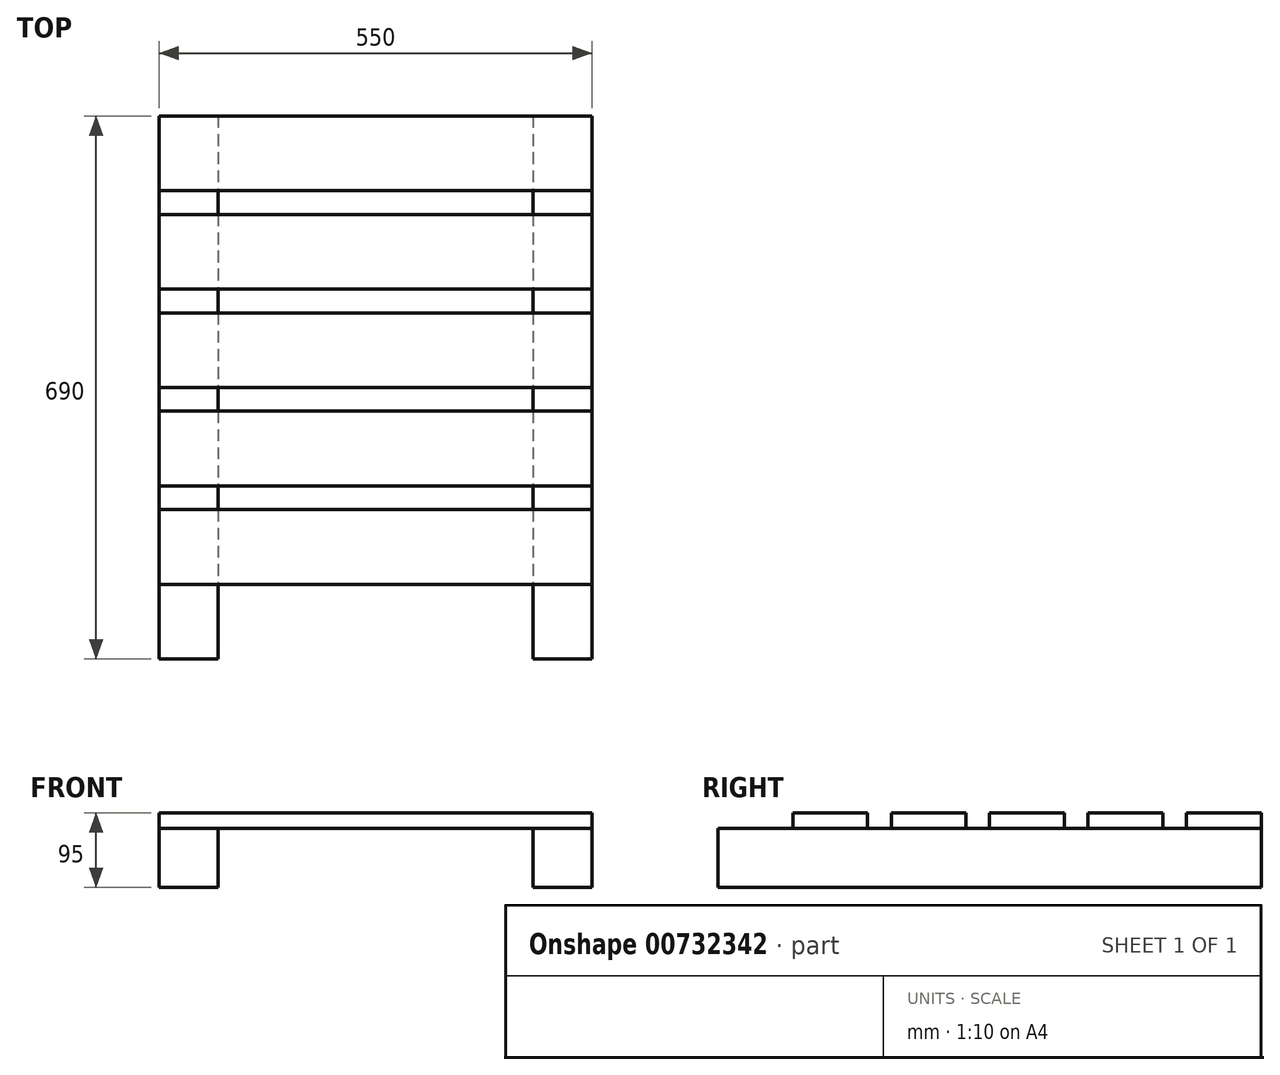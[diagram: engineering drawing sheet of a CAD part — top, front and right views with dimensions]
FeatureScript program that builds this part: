
annotation { "Feature Type Name" : "Feature", "Feature Type Description" : "" }
export const myFeature = defineFeature(function(context is Context, id is Id, definition is map)
    precondition{}
    {
        {
            var Q0;
            Q0=qCreatedBy(makeId("Top.planeOp"),FACE);
            var sketch = newSketch(context, id + "F0", { "sketchPlane" : qUnion([Q0])});
            skLineSegment(sketch, "E0.bottom", {"start": v(-275, -300) * mm, "end": v(275, -300) * mm, "construction": true});
            skLineSegment(sketch, "E0.top", {"start": v(-275, 300) * mm, "end": v(275, 300) * mm, "construction": true});
            skLineSegment(sketch, "E0.left", {"start": v(-275, -300) * mm, "end": v(-275, 300) * mm, "construction": true});
            skLineSegment(sketch, "E0.right", {"start": v(275, -300) * mm, "end": v(275, 300) * mm, "construction": true});
            skPoint(sketch, "E0.middle", {"position": v(0, 0) * mm});
            skLineSegment(sketch, "E1.bottom", {"start": v(-275, 300) * mm, "end": v(275, 300) * mm});
            skLineSegment(sketch, "E1.top", {"start": v(-275, 205) * mm, "end": v(275, 205) * mm});
            skLineSegment(sketch, "E1.left", {"start": v(-275, 300) * mm, "end": v(-275, 205) * mm});
            skLineSegment(sketch, "E1.right", {"start": v(275, 300) * mm, "end": v(275, 205) * mm});
            skLineSegment(sketch, "E2", {"start": v(-275, 205) * mm, "end": v(-275, 175) * mm, "construction": true});
            skLineSegment(sketch, "E3", {"start": v(-275, 175) * mm, "end": v(-275, 80) * mm, "construction": true});
            skLineSegment(sketch, "E4", {"start": v(-275, 80) * mm, "end": v(-275, 50) * mm, "construction": true});
            skLineSegment(sketch, "E5", {"start": v(-275, 50) * mm, "end": v(-275, -45) * mm, "construction": true});
            skLineSegment(sketch, "E6", {"start": v(-275, -45) * mm, "end": v(-275, -75) * mm, "construction": true});
            skLineSegment(sketch, "E7", {"start": v(-275, -75) * mm, "end": v(-275, -170) * mm, "construction": true});
            skLineSegment(sketch, "E8", {"start": v(-275, -170) * mm, "end": v(-275, -200) * mm, "construction": true});
            skLineSegment(sketch, "E9", {"start": v(-275, -200) * mm, "end": v(-275, -295) * mm, "construction": true});
            skLineSegment(sketch, "E10.bottom", {"start": v(-275, 175) * mm, "end": v(275, 175) * mm});
            skLineSegment(sketch, "E10.top", {"start": v(-275, 80) * mm, "end": v(275, 80) * mm});
            skLineSegment(sketch, "E10.left", {"start": v(-275, 175) * mm, "end": v(-275, 80) * mm});
            skLineSegment(sketch, "E10.right", {"start": v(275, 175) * mm, "end": v(275, 80) * mm});
            skLineSegment(sketch, "E11.bottom", {"start": v(-275, 50) * mm, "end": v(275, 50) * mm});
            skLineSegment(sketch, "E11.top", {"start": v(-275, -45) * mm, "end": v(275, -45) * mm});
            skLineSegment(sketch, "E11.left", {"start": v(-275, 50) * mm, "end": v(-275, -45) * mm});
            skLineSegment(sketch, "E11.right", {"start": v(275, 50) * mm, "end": v(275, -45) * mm});
            skLineSegment(sketch, "E12.bottom", {"start": v(-275, -75) * mm, "end": v(275, -75) * mm});
            skLineSegment(sketch, "E12.top", {"start": v(-275, -170) * mm, "end": v(275, -170) * mm});
            skLineSegment(sketch, "E12.left", {"start": v(-275, -75) * mm, "end": v(-275, -170) * mm});
            skLineSegment(sketch, "E12.right", {"start": v(275, -75) * mm, "end": v(275, -170) * mm});
            skLineSegment(sketch, "E13.bottom", {"start": v(-275, -200) * mm, "end": v(275, -200) * mm});
            skLineSegment(sketch, "E13.top", {"start": v(-275, -295) * mm, "end": v(275, -295) * mm});
            skLineSegment(sketch, "E13.left", {"start": v(-275, -200) * mm, "end": v(-275, -295) * mm});
            skLineSegment(sketch, "E13.right", {"start": v(275, -200) * mm, "end": v(275, -295) * mm});
            skSolve(sketch);
        }
        {
            var Q0;
            Q0=makeQuery(id+"F0.imprint","IMPRINT",FACE,{"disambiguationData":[TD([[makeQuery(id+"F0.imprint","IMPRINT",EDGE,{"derivedFrom":sQuery(id+"F0.wireOp",EDGE,"E1.bottom")}),-1.0]])]});
            var Q1;
            Q1=makeQuery(id+"F0.imprint","IMPRINT",FACE,{"disambiguationData":[TD([[makeQuery(id+"F0.imprint","IMPRINT",EDGE,{"derivedFrom":sQuery(id+"F0.wireOp",EDGE,"E10.bottom")}),-1.0]])]});
            var Q2;
            Q2=makeQuery(id+"F0.imprint","IMPRINT",FACE,{"disambiguationData":[TD([[makeQuery(id+"F0.imprint","IMPRINT",EDGE,{"derivedFrom":sQuery(id+"F0.wireOp",EDGE,"E11.bottom")}),-1.0]])]});
            var Q3;
            Q3=makeQuery(id+"F0.imprint","IMPRINT",FACE,{"disambiguationData":[TD([[makeQuery(id+"F0.imprint","IMPRINT",EDGE,{"derivedFrom":sQuery(id+"F0.wireOp",EDGE,"E12.bottom")}),-1.0]])]});
            var Q4;
            Q4=makeQuery(id+"F0.imprint","IMPRINT",FACE,{"disambiguationData":[TD([[makeQuery(id+"F0.imprint","IMPRINT",EDGE,{"derivedFrom":sQuery(id+"F0.wireOp",EDGE,"E13.bottom")}),-1.0]])]});
            extrude(context, id + "F1", {"entities" : qUnion([Q0, Q1, Q2, Q3, Q4]), "depth" : 20 * mm, "offsetDistance" : 25 * mm});
        }
        {
            var Q0;
            Q0=qCreatedBy(makeId("Top.planeOp"),FACE);
            var sketch = newSketch(context, id + "F2", { "sketchPlane" : qUnion([Q0])});
            skLineSegment(sketch, "E14.bottom", {"start": v(-200, 300) * mm, "end": v(-200, -390) * mm});
            skLineSegment(sketch, "E14.top", {"start": v(-275, 300) * mm, "end": v(-275, -390) * mm});
            skLineSegment(sketch, "E14.left", {"start": v(-200, 300) * mm, "end": v(-275, 300) * mm});
            skLineSegment(sketch, "E14.right", {"start": v(-200, -390) * mm, "end": v(-275, -390) * mm});
            skPoint(sketch, "E14.middle", {"position": v(-237.5, -45) * mm});
            skPoint(sketch, "E15.0", {"position": v(-275, 300) * mm});
            skLineSegment(sketch, "E16.bottom", {"start": v(275, 300) * mm, "end": v(275, -390) * mm});
            skLineSegment(sketch, "E16.top", {"start": v(200, 300) * mm, "end": v(200, -390) * mm});
            skLineSegment(sketch, "E16.left", {"start": v(275, 300) * mm, "end": v(200, 300) * mm});
            skLineSegment(sketch, "E16.right", {"start": v(275, -390) * mm, "end": v(200, -390) * mm});
            skPoint(sketch, "E16.middle", {"position": v(237.5, -45) * mm});
            skPoint(sketch, "E17.0", {"position": v(275, 300) * mm});
            skSolve(sketch);
        }
        {
            var Q0;
            Q0=makeQuery(id+"F2.imprint","IMPRINT",FACE,{"disambiguationData":[TD([[makeQuery(id+"F2.imprint","IMPRINT",EDGE,{"derivedFrom":sQuery(id+"F2.wireOp",EDGE,"E16.bottom")}),-1.0]])]});
            var Q1;
            Q1=makeQuery(id+"F2.imprint","IMPRINT",FACE,{"disambiguationData":[TD([[makeQuery(id+"F2.imprint","IMPRINT",EDGE,{"derivedFrom":sQuery(id+"F2.wireOp",EDGE,"E14.bottom")}),-1.0]])]});
            extrude(context, id + "F3", {"entities" : qUnion([Q0, Q1]), "oppositeDirection" : true, "depth" : 75 * mm, "offsetDistance" : 25 * mm});
        }
    });
